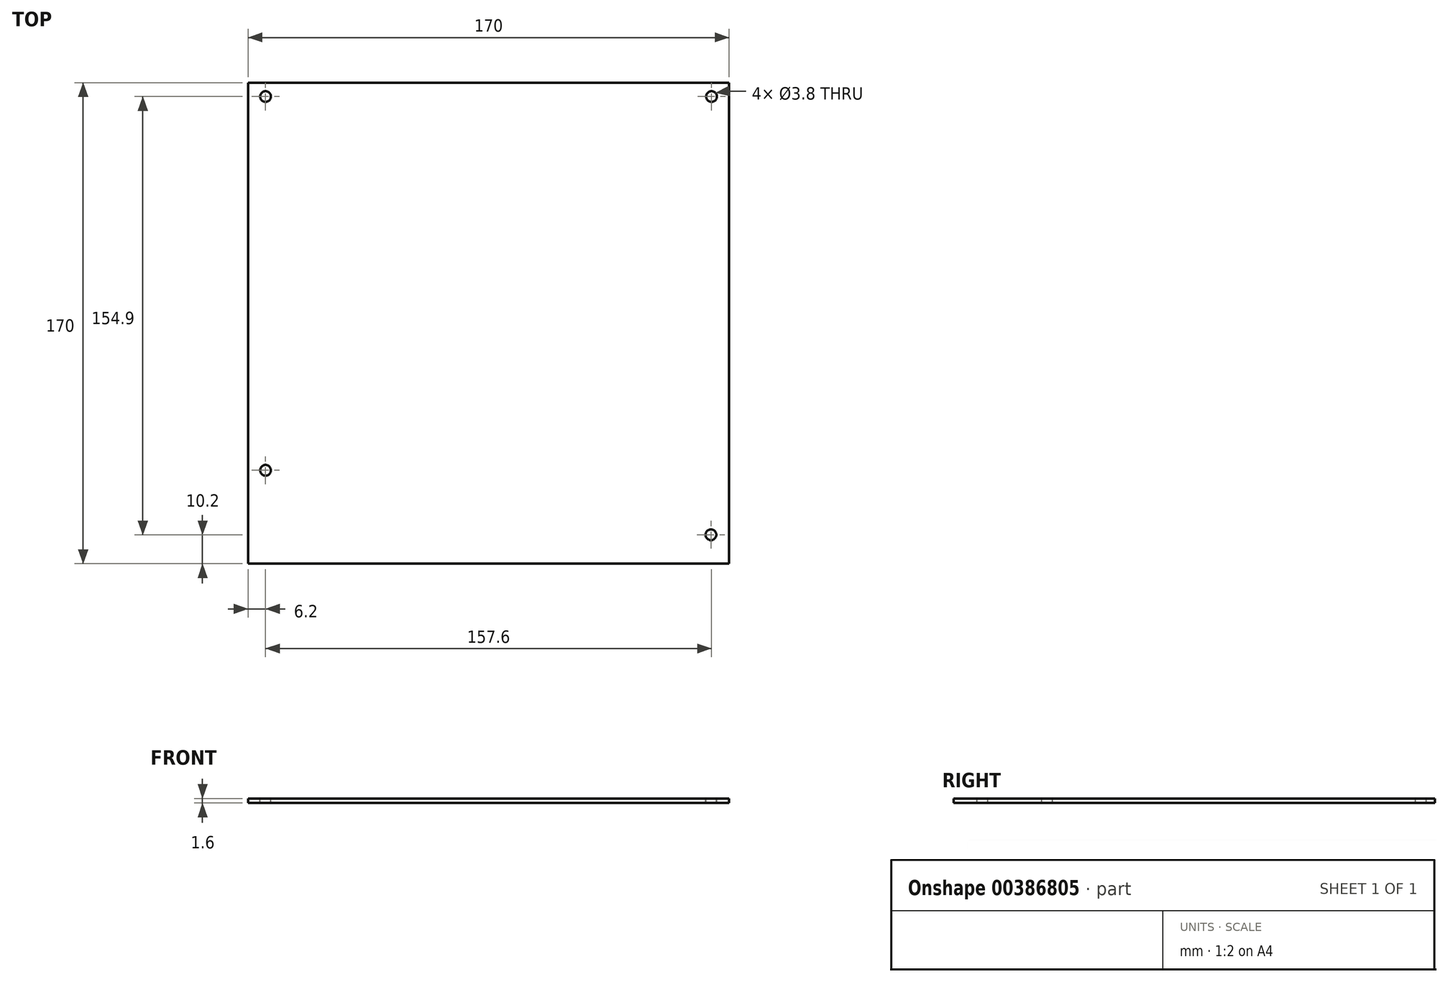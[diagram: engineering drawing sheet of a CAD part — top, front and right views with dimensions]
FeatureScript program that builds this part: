
annotation { "Feature Type Name" : "Feature", "Feature Type Description" : "" }
export const myFeature = defineFeature(function(context is Context, id is Id, definition is map)
    precondition{}
    {
        {
            var Q0;
            Q0=qCreatedBy(makeId("Top.planeOp"),FACE);
            var sketch = newSketch(context, id + "F0", { "sketchPlane" : qUnion([Q0])});
            skLineSegment(sketch, "E0.bottom", {"start": v(-85, 85) * mm, "end": v(85, 85) * mm});
            skLineSegment(sketch, "E0.top", {"start": v(-85, -85) * mm, "end": v(85, -85) * mm});
            skLineSegment(sketch, "E0.left", {"start": v(-85, 85) * mm, "end": v(-85, -85) * mm});
            skLineSegment(sketch, "E0.right", {"start": v(85, 85) * mm, "end": v(85, -85) * mm});
            skPoint(sketch, "E1", {"position": v(-78.8, 80.1) * mm});
            skPoint(sketch, "E2", {"position": v(78.8, 80.1) * mm});
            skPoint(sketch, "E3", {"position": v(78.6, -74.8) * mm});
            skPoint(sketch, "E4", {"position": v(-78.8, -52) * mm});
            skSolve(sketch);
        }
        {
            var Q0;
            Q0=makeQuery(id+"F0.imprint","IMPRINT",FACE,{"disambiguationData":[TD([[makeQuery(id+"F0.imprint","IMPRINT",EDGE,{"derivedFrom":sQuery(id+"F0.wireOp",EDGE,"E0.bottom")}),-1.0]])]});
            extrude(context, id + "F1", {"entities" : qUnion([Q0]), "oppositeDirection" : true, "depth" : 1.6 * mm});
        }
        {
            var Q0;
            Q0=sQuery(id+"F0.wireOp",VERTEX,"E2");
            var Q1;
            Q1=sQuery(id+"F0.wireOp",VERTEX,"E3");
            var Q2;
            Q2=sQuery(id+"F0.wireOp",VERTEX,"E4");
            var Q3;
            Q3=sQuery(id+"F0.wireOp",VERTEX,"E1");
            var Q4;
            Q4=makeQuery(id+"F1.opExtrude","SWEPT_BODY",BODY,{"disambiguationData":[OSD([sQuery(id+"F0.wireOp",EDGE,"E0.bottom"),sQuery(id+"F0.wireOp",EDGE,"E0.top"),sQuery(id+"F0.wireOp",EDGE,"E0.left"),sQuery(id+"F0.wireOp",EDGE,"E0.right")])]});
            hole(context, id + "F2", {"style" : HoleStyle.SIMPLE, "endStyle" : HoleEndStyle.THROUGH, "holeDiameter" : 3.8 * mm, "isTappedThrough" : true, "tappedDepth" : 12 * mm, "tapClearance" : 3, "locations" : qUnion([Q0, Q1, Q2, Q3]), "scope" : qUnion([Q4])});
        }
    });
